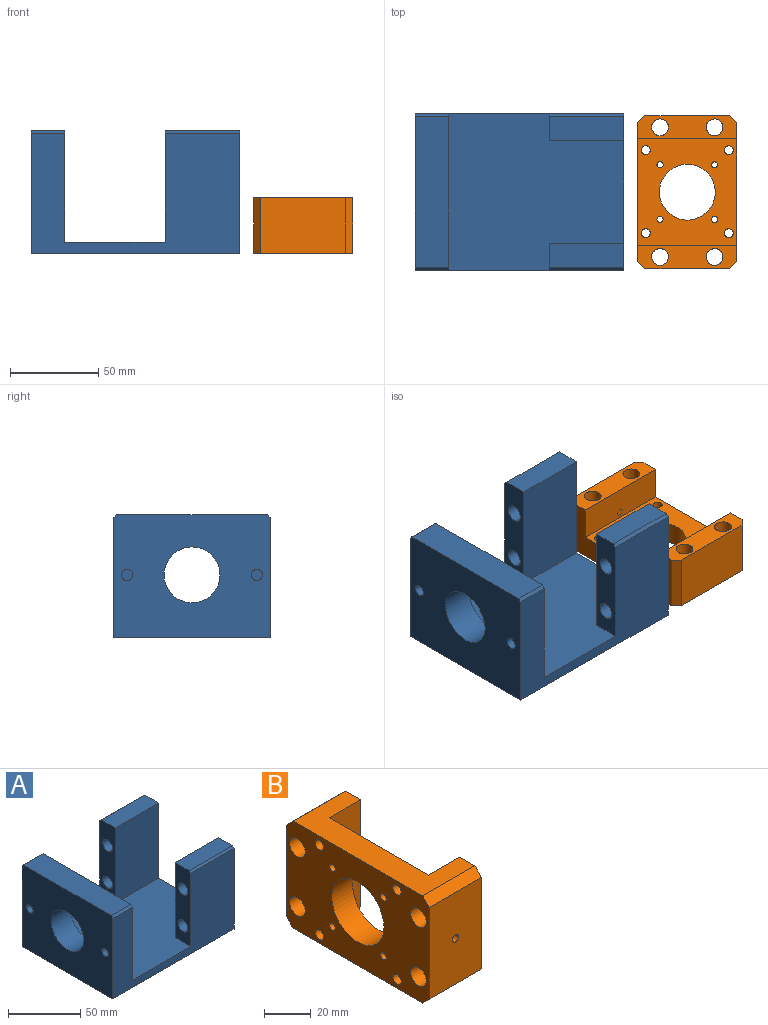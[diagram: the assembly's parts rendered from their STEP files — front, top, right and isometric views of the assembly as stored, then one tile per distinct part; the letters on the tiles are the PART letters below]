
ASSEMBLY  parts=2 mates=1
PART A: 73 faces, bbox 118.5x88.9x69.9 mm
  f0: plane 118.47x68.27mm, normal (0,-1,0), area 4549.3mm2, adj f12,f14,f15,f16,f17,f22,f23,f25
  f1: plane 118.47x68.27mm, normal (0,1,0), area 4549.3mm2, adj f12,f14,f15,f16,f17,f20,f21,f24
  f2: plane 60.33x27.62mm, normal (1,0,0), area 858.1mm2, adj f3,f4,f12,f45,f47,f50,f51,f55
  f3: cylinder r=19.69mm len=19.34mm, axis (-1,0,0), area 173mm2, adj f2,f14,f45,f55
  f4: plane 55.25x6.35mm, normal (0,-1,0), area 350.8mm2, adj f2,f14,f51,f60
  f5: cylinder r=3.17mm len=16.87mm, axis (1,0,0), area 336.6mm2, adj f16,f33
  f6: cylinder r=3.17mm len=16.87mm, axis (1,0,0), area 336.6mm2, adj f16,f31
  f7: cylinder r=3.17mm len=16.87mm, axis (1,0,0), area 336.6mm2, adj f16,f28
  f8: cylinder r=3.17mm len=16.87mm, axis (1,0,0), area 336.6mm2, adj f16,f26
  f9: plane 63.51x42.27mm, normal (0,1,0), area 2684.5mm2, adj f11,f12,f16,f25
  f10: plane 63.51x42.27mm, normal (0,-1,0), area 2684.5mm2, adj f12,f16,f19,f24
  f11: plane 42.27x13.65mm, normal (0,0,1), area 577.1mm2, adj f9,f16,f22,f25
  f12: plane 105.77x88.9mm, normal (0,0,1), area 7606.6mm2, adj f0,f1,f2,f9,f10,f14,f16,f24
  f13: plane 55.25x6.35mm, normal (0,1,0), area 350.8mm2, adj f14,f43,f52,f59
  f14: plane 88.9x63.51mm, normal (1,0,0), area 3008.5mm2, adj f0,f1,f3,f4,f12,f13,f18,f20
  f15: plane 88.9x69.86mm, normal (-1,0,0), area 5352.6mm2, adj f0,f1,f17,f18,f20,f23,f42,f69
  f16: plane 88.9x69.86mm, normal (1,0,0), area 2339.3mm2, adj f0,f1,f5,f6,f7,f8,f9,f10
  f17: plane 118.47x88.9mm, normal (0,0,-1), area 10532.2mm2, adj f0,f1,f15,f16
  f18: plane 85.73x19.05mm, normal (0,0,1), area 1633.1mm2, adj f14,f15,f20,f23
  f19: plane 42.27x13.65mm, normal (0,0,1), area 577.1mm2, adj f10,f16,f21,f24
  f20: plane 19.05x1.59mm, normal (0,0.71,0.71), area 42.8mm2, adj f1,f14,f15,f18
  f21: plane 42.27x1.59mm, normal (0,0.71,0.71), area 94.9mm2, adj f1,f16,f19,f24
  f22: plane 42.27x1.59mm, normal (0,-0.71,0.71), area 94.9mm2, adj f0,f11,f16,f25
  f23: plane 19.05x1.59mm, normal (0,-0.71,0.71), area 42.8mm2, adj f0,f14,f15,f18
  f24: plane 63.51x15.24mm, normal (-1,0,0), area 824.1mm2, adj f1,f10,f12,f19,f21,f27,f29
  f25: plane 63.51x15.24mm, normal (-1,0,0), area 824.1mm2, adj f0,f9,f11,f12,f22,f30,f32
  f26: plane 9.53x9.53mm, normal (-1,0,0), area 39.6mm2, adj f8,f27
  f27: cylinder r=4.76mm len=25.4mm, axis (-1,0,0), area 760.1mm2, adj f24,f26
  f28: plane 9.53x9.53mm, normal (-1,0,0), area 39.6mm2, adj f7,f29
  f29: cylinder r=4.76mm len=25.4mm, axis (-1,0,0), area 760.1mm2, adj f24,f28
  f30: cylinder r=4.76mm len=25.4mm, axis (-1,0,0), area 760.1mm2, adj f25,f31
  f31: plane 9.53x9.53mm, normal (-1,0,0), area 39.6mm2, adj f6,f30
  f32: cylinder r=4.76mm len=25.4mm, axis (-1,0,0), area 760.1mm2, adj f25,f33
  f33: plane 9.53x9.53mm, normal (-1,0,0), area 39.6mm2, adj f5,f32
  f34: cylinder r=1.59mm len=12.7mm, axis (1,0,0), area 126.7mm2, adj f16,f35
  f35: plane 3.18x3.18mm, normal (1,0,0), area 7.9mm2, adj f34
  f36: cylinder r=1.59mm len=12.7mm, axis (1,0,0), area 126.7mm2, adj f16,f37
  f37: plane 3.18x3.18mm, normal (1,0,0), area 7.9mm2, adj f36
  f38: cylinder r=1.59mm len=12.7mm, axis (1,0,0), area 126.7mm2, adj f16,f39
  f39: plane 3.18x3.18mm, normal (1,0,0), area 7.9mm2, adj f38
  f40: cylinder r=1.59mm len=12.7mm, axis (1,0,0), area 126.7mm2, adj f16,f41
  f41: plane 3.18x3.18mm, normal (1,0,0), area 7.9mm2, adj f40
  f42: cylinder r=15.88mm len=31.75mm, axis (-1,0,0), area 1900.2mm2, adj f14,f15
  f43: plane 60.33x27.62mm, normal (1,0,0), area 858.1mm2, adj f12,f13,f44,f46,f48,f49,f52,f53
  f44: cylinder r=19.69mm len=19.34mm, axis (-1,0,0), area 173mm2, adj f14,f43,f46,f54
  f45: plane 26.68x6.35mm, normal (0,1,0), area 169.4mm2, adj f2,f3,f14,f58
  f46: plane 26.68x6.35mm, normal (0,-1,0), area 169.4mm2, adj f14,f43,f44,f57
  f47: plane 22.54x6.35mm, normal (0,0,-1), area 143.1mm2, adj f2,f14,f51,f56
  f48: plane 22.54x6.35mm, normal (0,0,-1), area 143.1mm2, adj f14,f43,f52,f53
  f49: plane 6.74x6.35mm, normal (0,-1,0), area 42.8mm2, adj f14,f43,f53,f54
  f50: plane 6.74x6.35mm, normal (0,1,0), area 42.8mm2, adj f2,f14,f55,f56
  f51: cylinder r=2.54mm len=6.35mm, axis (-1,0,0), area 25.3mm2, adj f2,f4,f14,f47
  f52: cylinder r=2.54mm len=6.35mm, axis (1,0,0), area 25.3mm2, adj f13,f14,f43,f48
  f53: cylinder r=2.54mm len=6.35mm, axis (1,0,0), area 25.3mm2, adj f14,f43,f48,f49
  f54: cylinder r=2.54mm len=6.35mm, axis (-1,0,0), area 22.3mm2, adj f14,f43,f44,f49
  f55: cylinder r=2.54mm len=6.35mm, axis (-1,0,0), area 22.3mm2, adj f2,f3,f14,f50
  f56: cylinder r=2.54mm len=6.35mm, axis (1,0,0), area 25.3mm2, adj f2,f14,f47,f50
  f57: cylinder r=2.54mm len=6.35mm, axis (-1,0,0), area 25.3mm2, adj f12,f14,f43,f46
  f58: cylinder r=2.54mm len=6.35mm, axis (-1,0,0), area 25.3mm2, adj f2,f12,f14,f45
  f59: cylinder r=2.54mm len=6.35mm, axis (-1,0,0), area 25.3mm2, adj f12,f13,f14,f43
  f60: cylinder r=2.54mm len=6.35mm, axis (1,0,0), area 25.3mm2, adj f2,f4,f12,f14
  f61: cylinder r=3.17mm len=12.7mm, axis (1,0,0), area 253.4mm2, adj f14,f62
  f62: plane 6.35x6.35mm, normal (1,0,0), area 31.7mm2, adj f61
  f63: cylinder r=3.17mm len=12.7mm, axis (1,0,0), area 253.4mm2, adj f14,f64
  f64: plane 6.35x6.35mm, normal (1,0,0), area 31.7mm2, adj f63
  f65: cylinder r=3.17mm len=12.7mm, axis (1,0,0), area 253.4mm2, adj f14,f66
  f66: plane 6.35x6.35mm, normal (1,0,0), area 31.7mm2, adj f65
  f67: cylinder r=3.17mm len=12.7mm, axis (1,0,0), area 253.4mm2, adj f14,f68
  f68: plane 6.35x6.35mm, normal (1,0,0), area 31.7mm2, adj f67
  f69: cylinder r=3.17mm len=12.7mm, axis (-1,0,0), area 253.4mm2, adj f15,f70
  f70: plane 6.35x6.35mm, normal (-1,0,0), area 31.7mm2, adj f69
  f71: cylinder r=3.17mm len=12.7mm, axis (-1,0,0), area 253.4mm2, adj f15,f72
  f72: plane 6.35x6.35mm, normal (-1,0,0), area 31.7mm2, adj f71
PART B: 29 faces, bbox 31.8x86.9x56.4 mm
  f0: plane 86.87x56.4mm, normal (-1,0,0), area 3669.9mm2, adj f2,f4,f5,f7,f8,f9,f10,f11
  f1: plane 60.43x56.4mm, normal (1,0,0), area 2496.7mm2, adj f2,f3,f6,f9,f10,f11,f12,f13
  f2: plane 78.74x31.75mm, normal (0,0,1), area 1348.9mm2, adj f0,f1,f3,f5,f6,f7,f21,f22
  f3: plane 56.4x19.05mm, normal (0,-1,0), area 1074.4mm2, adj f1,f2,f9,f22
  f4: plane 48.27x31.75mm, normal (0,1,0), area 1532.6mm2, adj f0,f5,f16,f22
  f5: plane 31.75x4.06mm, normal (0,0.71,0.71), area 182.5mm2, adj f0,f2,f4,f22
  f6: plane 56.4x19.05mm, normal (0,1,0), area 1074.4mm2, adj f1,f2,f9,f21
  f7: plane 31.75x4.06mm, normal (0,-0.71,0.71), area 182.5mm2, adj f0,f2,f8,f21
  f8: plane 48.27x31.75mm, normal (0,-1,0), area 1521.2mm2, adj f0,f7,f14,f21,f23
  f9: plane 78.74x31.75mm, normal (0,0,-1), area 1348.9mm2, adj f0,f1,f3,f6,f14,f16,f21,f22
  f10: cylinder r=2.54mm len=12.7mm, axis (1,0,0), area 202.7mm2, adj f0,f1
  f11: cylinder r=2.54mm len=12.7mm, axis (1,0,0), area 202.7mm2, adj f0,f1
  f12: cylinder r=2.54mm len=12.7mm, axis (1,0,0), area 202.7mm2, adj f0,f1
  f13: cylinder r=2.54mm len=12.7mm, axis (1,0,0), area 202.7mm2, adj f0,f1
  f14: plane 31.75x4.06mm, normal (0,-0.71,-0.71), area 182.5mm2, adj f0,f8,f9,f21
  f15: cylinder r=4.76mm len=31.75mm, axis (1,0,0), area 950.1mm2, adj f0,f21
  f16: plane 31.75x4.06mm, normal (0,0.71,-0.71), area 182.5mm2, adj f0,f4,f9,f22
  f17: cylinder r=4.76mm len=31.75mm, axis (1,0,0), area 950.1mm2, adj f0,f22
  f18: cylinder r=4.76mm len=31.75mm, axis (1,0,0), area 950.1mm2, adj f0,f21
  f19: cylinder r=4.76mm len=31.75mm, axis (1,0,0), area 950.1mm2, adj f0,f22
  f20: cylinder r=15.88mm len=31.75mm, axis (-1,0,0), area 1266.8mm2, adj f0,f1
  f21: plane 56.4x13.22mm, normal (1,0,0), area 586.6mm2, adj f2,f6,f7,f8,f9,f14,f15,f18
  f22: plane 56.4x13.22mm, normal (1,0,0), area 586.6mm2, adj f2,f3,f4,f5,f9,f16,f17,f19
  f23: cylinder r=1.91mm len=12.7mm, axis (0,-1,0), area 152mm2, adj f8,f24
  f24: plane 3.81x3.81mm, normal (0,-1,0), area 11.4mm2, adj f23
  f25: cylinder r=1.75mm len=12.7mm, axis (-1,0,0), area 139.6mm2, adj f0,f1
  f26: cylinder r=1.75mm len=12.7mm, axis (-1,0,0), area 139.9mm2, adj f0,f1
  f27: cylinder r=1.75mm len=12.7mm, axis (-1,0,0), area 139.9mm2, adj f0,f1
  f28: cylinder r=1.75mm len=12.7mm, axis (-1,0,0), area 139.9mm2, adj f0,f1
PLACE A at identity fixed
PLACE B rot(axis=(0.71,0,0.71),180deg) t=(204.47,-0.04,-104.42)mm
MATE planar A.f17 <-> B.f20  axis (0,0,-1) through (109.04,0,-35.57)mm
